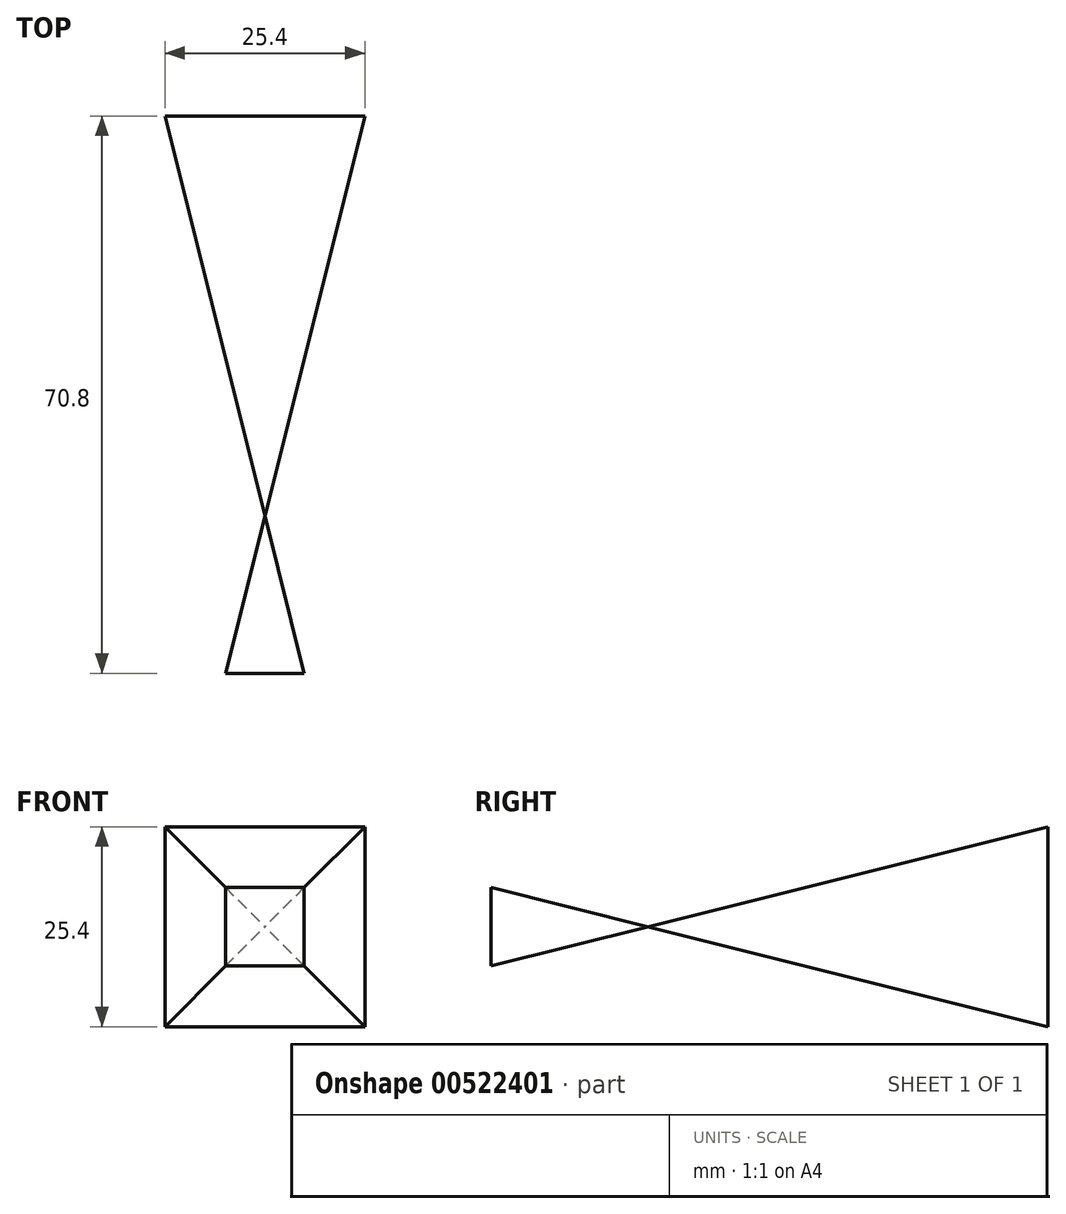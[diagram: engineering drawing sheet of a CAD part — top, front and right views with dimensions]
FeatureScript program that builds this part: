
annotation { "Feature Type Name" : "Feature", "Feature Type Description" : "" }
export const myFeature = defineFeature(function(context is Context, id is Id, definition is map)
    precondition{}
    {
        {
            var Q0;
            Q0=qCreatedBy(makeId("Front.planeOp"),FACE);
            var sketch = newSketch(context, id + "F0", { "sketchPlane" : qUnion([Q0])});
            skPoint(sketch, "E0", {"position": v(0, 0) * mm});
            skSolve(sketch);
        }
        {
            var Q0;
            Q0=qCreatedBy(makeId("Front.planeOp"),FACE);
            cPlane(context, id + "F1", {"entities" : qUnion([Q0]), "cplaneType" : CPlaneType.OFFSET, "offset" : 20 * mm, "width" : 152.4 * mm, "height" : 152.4 * mm});
        }
        {
            var Q0;
            Q0=qCreatedBy(id+"F1.planeOp",FACE);
            var sketch = newSketch(context, id + "F2", { "sketchPlane" : qUnion([Q0])});
            skLineSegment(sketch, "E1.bottom", {"start": v(-5, 5) * mm, "end": v(5, 5) * mm});
            skLineSegment(sketch, "E1.top", {"start": v(-5, -5) * mm, "end": v(5, -5) * mm});
            skLineSegment(sketch, "E1.left", {"start": v(-5, 5) * mm, "end": v(-5, -5) * mm});
            skLineSegment(sketch, "E1.right", {"start": v(5, 5) * mm, "end": v(5, -5) * mm});
            skLineSegment(sketch, "E2", {"start": v(-5, 0) * mm, "end": v(5, 0) * mm, "construction": true});
            skLineSegment(sketch, "E3", {"start": v(0, 5) * mm, "end": v(0, -5) * mm, "construction": true});
            skSolve(sketch);
        }
        {
            var Q0;
            Q0=qCreatedBy(makeId("Front.planeOp"),FACE);
            cPlane(context, id + "F3", {"entities" : qUnion([Q0]), "cplaneType" : CPlaneType.OFFSET, "offset" : 50.8 * mm, "oppositeDirection" : true, "width" : 152.4 * mm, "height" : 152.4 * mm});
        }
        {
            var Q0;
            Q0=sQuery(id+"F2.wireOp",VERTEX,"E1.right.start");
            var Q1;
            Q1=sQuery(id+"F2.wireOp",VERTEX,"E1.right.end");
            var Q2;
            Q2=sQuery(id+"F0.wireOp",VERTEX,"E0");
            cPlane(context, id + "F4", {"entities" : qUnion([Q0, Q1, Q2]), "cplaneType" : CPlaneType.THREE_POINT, "offset" : 25.4 * mm, "width" : 152.4 * mm, "height" : 152.4 * mm});
        }
        {
            var Q0;
            Q0=sQuery(id+"F2.wireOp",VERTEX,"E1.right.start");
            var Q1;
            Q1=sQuery(id+"F2.wireOp",VERTEX,"E1.left.start");
            var Q2;
            Q2=sQuery(id+"F0.wireOp",VERTEX,"E0");
            cPlane(context, id + "F5", {"entities" : qUnion([Q0, Q1, Q2]), "cplaneType" : CPlaneType.THREE_POINT, "offset" : 25.4 * mm, "width" : 152.4 * mm, "height" : 152.4 * mm});
        }
        {
            var Q0;
            Q0=qCreatedBy(id+"F3.planeOp",FACE);
            var sketch = newSketch(context, id + "F6", { "sketchPlane" : qUnion([Q0])});
            skLineSegment(sketch, "E4.bottom", {"start": v(-12.7, 12.7) * mm, "end": v(12.7, 12.7) * mm});
            skLineSegment(sketch, "E4.top", {"start": v(-12.7, -12.7) * mm, "end": v(12.7, -12.7) * mm});
            skLineSegment(sketch, "E4.left", {"start": v(-12.7, 12.7) * mm, "end": v(-12.7, -12.7) * mm});
            skLineSegment(sketch, "E4.right", {"start": v(12.7, 12.7) * mm, "end": v(12.7, -12.7) * mm});
            skLineSegment(sketch, "E5", {"start": v(-12.7, 0) * mm, "end": v(12.7, 0) * mm, "construction": true});
            skLineSegment(sketch, "E6", {"start": v(0, 12.7) * mm, "end": v(0, -12.7) * mm, "construction": true});
            skSolve(sketch);
        }
        {
            var Q0;
            Q0=makeQuery(id+"F2.imprint","IMPRINT",FACE,{"disambiguationData":[TD([[makeQuery(id+"F2.imprint","IMPRINT",EDGE,{"derivedFrom":sQuery(id+"F2.wireOp",EDGE,"E1.bottom")}),-1.0]])]});
            var Q1;
            Q1=sQuery(id+"F0.wireOp",VERTEX,"E0");
            loft(context, id + "F7", {"sheetProfilesArray" : [{ "sheetProfileEntities" : qUnion([Q0]) }, { "sheetProfileEntities" : qUnion([Q1]) }]});
        }
        {
            var Q0;
            Q0=qCreatedBy(makeId("Origin.pointOp"),VERTEX);
            var Q1;
            Q1=makeQuery(id+"F6.imprint","IMPRINT",FACE,{"disambiguationData":[TD([[makeQuery(id+"F6.imprint","IMPRINT",EDGE,{"derivedFrom":sQuery(id+"F6.wireOp",EDGE,"E4.bottom")}),-1.0]])]});
            loft(context, id + "F8", {"sheetProfilesArray" : [{ "sheetProfileEntities" : qUnion([Q0]) }, { "sheetProfileEntities" : qUnion([Q1]) }]});
        }
    });
